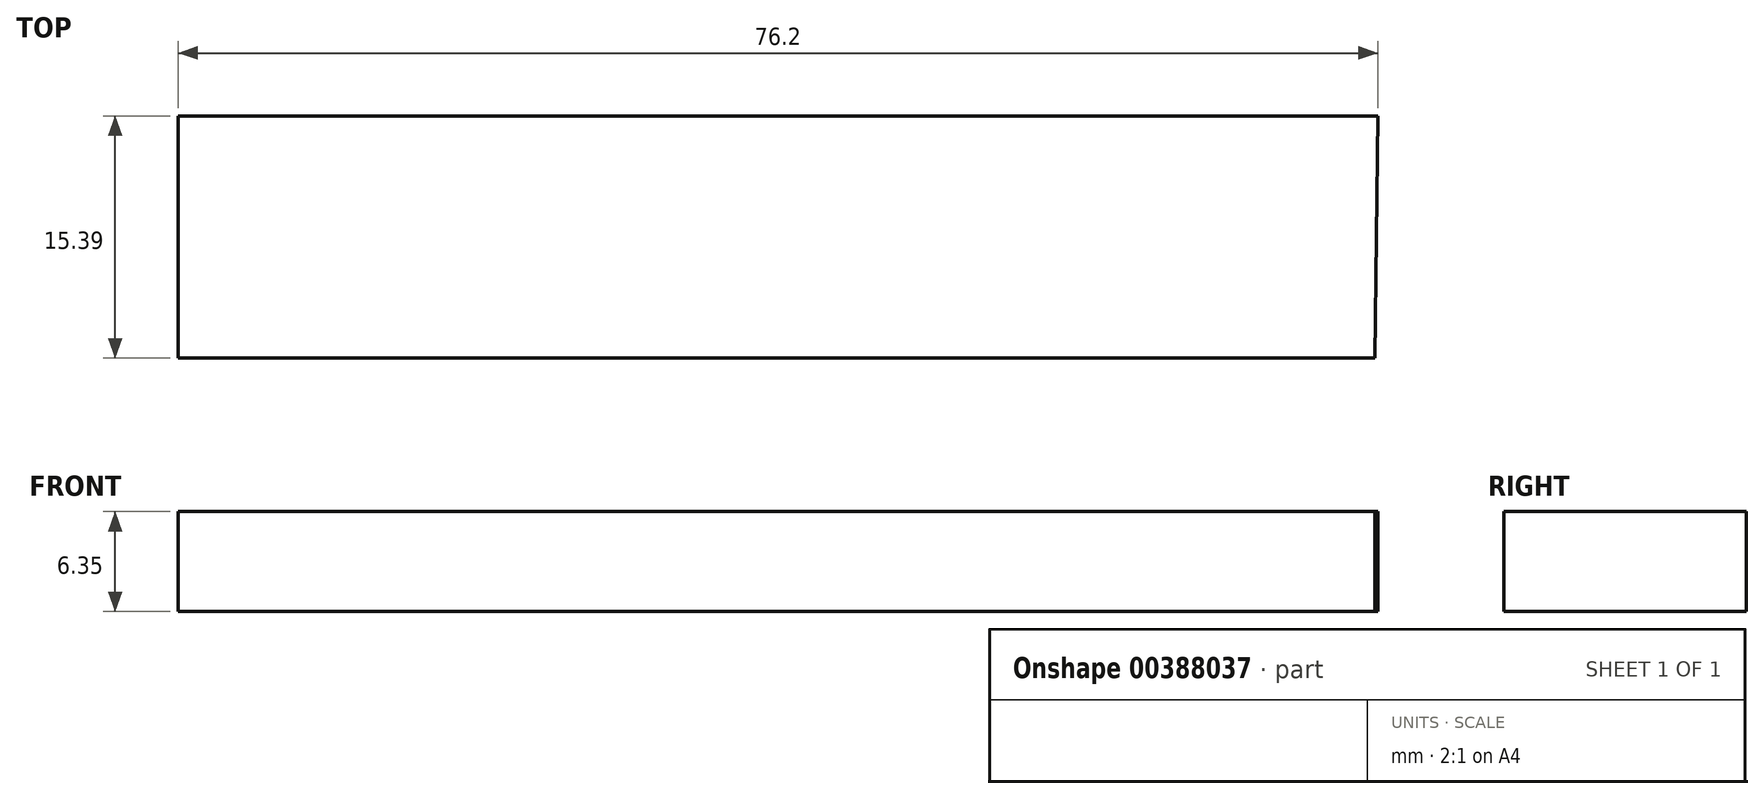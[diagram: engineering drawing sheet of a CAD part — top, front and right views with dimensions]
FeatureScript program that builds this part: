
annotation { "Feature Type Name" : "Feature", "Feature Type Description" : "" }
export const myFeature = defineFeature(function(context is Context, id is Id, definition is map)
    precondition{}
    {
        {
            var Q0;
            Q0=qCreatedBy(makeId("Top.planeOp"),FACE);
            var sketch = newSketch(context, id + "F0", { "sketchPlane" : qUnion([Q0])});
            skLineSegment(sketch, "E0", {"start": v(0, 0) * mm, "end": v(76.2, 0) * mm});
            skLineSegment(sketch, "E1", {"start": v(0, 0) * mm, "end": v(0, -15.4) * mm});
            skLineSegment(sketch, "E2", {"start": v(0, -15.4) * mm, "end": v(76.01, -15.4) * mm});
            skLineSegment(sketch, "E3", {"start": v(76.2, 0) * mm, "end": v(76.01, -15.4) * mm});
            skSolve(sketch);
        }
        {
            var Q0;
            Q0 = qSketchRegion(id + "F0", true);
            extrude(context, id + "F1", {"entities" : qUnion([Q0]), "depth" : 6.35 * mm});
        }
    });
